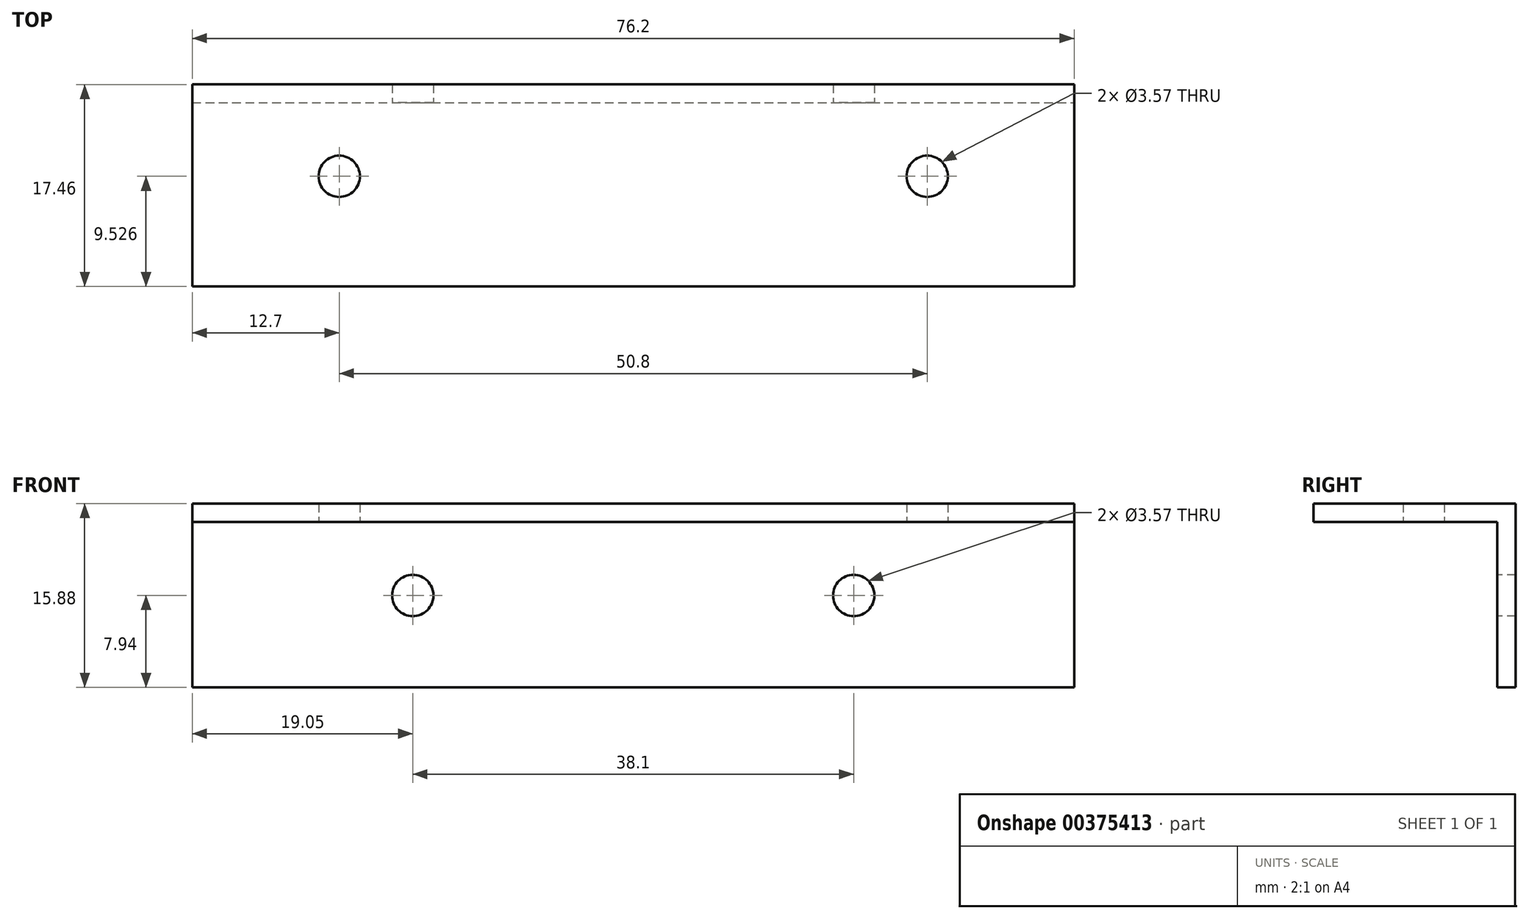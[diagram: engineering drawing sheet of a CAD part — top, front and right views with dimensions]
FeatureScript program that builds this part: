
annotation { "Feature Type Name" : "Feature", "Feature Type Description" : "" }
export const myFeature = defineFeature(function(context is Context, id is Id, definition is map)
    precondition{}
    {
        {
            var Q0;
            Q0=qCreatedBy(makeId("Front.planeOp"),FACE);
            var sketch = newSketch(context, id + "F0", { "sketchPlane" : qUnion([Q0])});
            skLineSegment(sketch, "E0.bottom", {"start": v(-38.1, 7.94) * mm, "end": v(38.1, 7.94) * mm});
            skLineSegment(sketch, "E0.top", {"start": v(-38.1, -7.94) * mm, "end": v(38.1, -7.94) * mm});
            skLineSegment(sketch, "E0.left", {"start": v(-38.1, 7.94) * mm, "end": v(-38.1, -7.94) * mm});
            skLineSegment(sketch, "E0.right", {"start": v(38.1, 7.94) * mm, "end": v(38.1, -7.94) * mm});
            skPoint(sketch, "E0.middle", {"position": v(0, 0) * mm});
            skSolve(sketch);
        }
        {
            var Q0;
            Q0=qSketchRegion(id+"F0",true);
            extrude(context, id + "F1", {"entities" : qUnion([Q0]), "depth" : 1.59 * mm, "symmetric" : true});
        }
        {
            var Q0;
            Q0=makeQuery(id+"F1.opExtrude","CAP_FACE",FACE,{"disambiguationData":[OSD([sQuery(id+"F0.wireOp",EDGE,"E0.bottom"),sQuery(id+"F0.wireOp",EDGE,"E0.top"),sQuery(id+"F0.wireOp",EDGE,"E0.left"),sQuery(id+"F0.wireOp",EDGE,"E0.right")])],"isStart":false});
            var sketch = newSketch(context, id + "F2", { "sketchPlane" : qUnion([Q0])});
            skCircle(sketch, "E1", {"center": v(-19.05, 0) * mm, "radius": 1.79 * mm});
            skSolve(sketch);
        }
        {
            var Q0;
            Q0=qSketchRegion(id+"F2",true);
            extrude(context, id + "F3", {"entities" : qUnion([Q0]), "operationType" : NewBodyOperationType.REMOVE, "endBound" : BoundingType.THROUGH_ALL, "oppositeDirection" : true, "depth" : 25.4 * mm});
        }
        {
            var Q0;
            Q0=makeQuery(id+"F1.opExtrude","CAP_FACE",FACE,{"disambiguationData":[OSD([sQuery(id+"F0.wireOp",EDGE,"E0.bottom"),sQuery(id+"F0.wireOp",EDGE,"E0.top"),sQuery(id+"F0.wireOp",EDGE,"E0.left"),sQuery(id+"F0.wireOp",EDGE,"E0.right")])],"isStart":false});
            var sketch = newSketch(context, id + "F4", { "sketchPlane" : qUnion([Q0])});
            skCircle(sketch, "E2", {"center": v(19.05, 0) * mm, "radius": 1.79 * mm});
            skSolve(sketch);
        }
        {
            var Q0;
            Q0=qSketchRegion(id+"F4",true);
            extrude(context, id + "F5", {"entities" : qUnion([Q0]), "operationType" : NewBodyOperationType.REMOVE, "endBound" : BoundingType.THROUGH_ALL, "oppositeDirection" : true, "depth" : 25.4 * mm});
        }
        {
            var Q0;
            Q0=makeQuery(id+"F1.opExtrude","CAP_FACE",FACE,{"disambiguationData":[OSD([sQuery(id+"F0.wireOp",EDGE,"E0.bottom"),sQuery(id+"F0.wireOp",EDGE,"E0.top"),sQuery(id+"F0.wireOp",EDGE,"E0.left"),sQuery(id+"F0.wireOp",EDGE,"E0.right")])],"isStart":false});
            var sketch = newSketch(context, id + "F6", { "sketchPlane" : qUnion([Q0])});
            skLineSegment(sketch, "E3.bottom", {"start": v(-38.1, 7.94) * mm, "end": v(38.1, 7.94) * mm});
            skLineSegment(sketch, "E3.top", {"start": v(-38.1, 6.35) * mm, "end": v(38.1, 6.35) * mm});
            skLineSegment(sketch, "E3.left", {"start": v(-38.1, 7.94) * mm, "end": v(-38.1, 6.35) * mm});
            skLineSegment(sketch, "E3.right", {"start": v(38.1, 7.94) * mm, "end": v(38.1, 6.35) * mm});
            skSolve(sketch);
        }
        {
            var Q0;
            Q0=qSketchRegion(id+"F6",true);
            extrude(context, id + "F7", {"entities" : qUnion([Q0]), "operationType" : NewBodyOperationType.ADD, "depth" : 15.88 * mm});
        }
        {
            var Q0;
            Q0=makeQuery(id+"F7.opExtrude","SWEPT_FACE",FACE,{"disambiguationData":[OSD([sQuery(id+"F6.wireOp",EDGE,"E3.top")])]});
            var sketch = newSketch(context, id + "F8", { "sketchPlane" : qUnion([Q0])});
            skCircle(sketch, "E4", {"center": v(-25.4, 7.14) * mm, "radius": 1.79 * mm});
            skSolve(sketch);
        }
        {
            var Q0;
            Q0=qSketchRegion(id+"F8",true);
            extrude(context, id + "F9", {"entities" : qUnion([Q0]), "operationType" : NewBodyOperationType.REMOVE, "endBound" : BoundingType.THROUGH_ALL, "oppositeDirection" : true, "depth" : 25.4 * mm});
        }
        {
            var Q0;
            Q0=makeQuery(id+"F7.opExtrude","SWEPT_FACE",FACE,{"disambiguationData":[OSD([sQuery(id+"F6.wireOp",EDGE,"E3.top")])]});
            var sketch = newSketch(context, id + "F10", { "sketchPlane" : qUnion([Q0])});
            skCircle(sketch, "E5", {"center": v(25.4, 7.14) * mm, "radius": 1.79 * mm});
            skSolve(sketch);
        }
        {
            var Q0;
            Q0=qSketchRegion(id+"F10",true);
            extrude(context, id + "F11", {"entities" : qUnion([Q0]), "operationType" : NewBodyOperationType.REMOVE, "endBound" : BoundingType.THROUGH_ALL, "oppositeDirection" : true, "depth" : 25.4 * mm});
        }
    });
